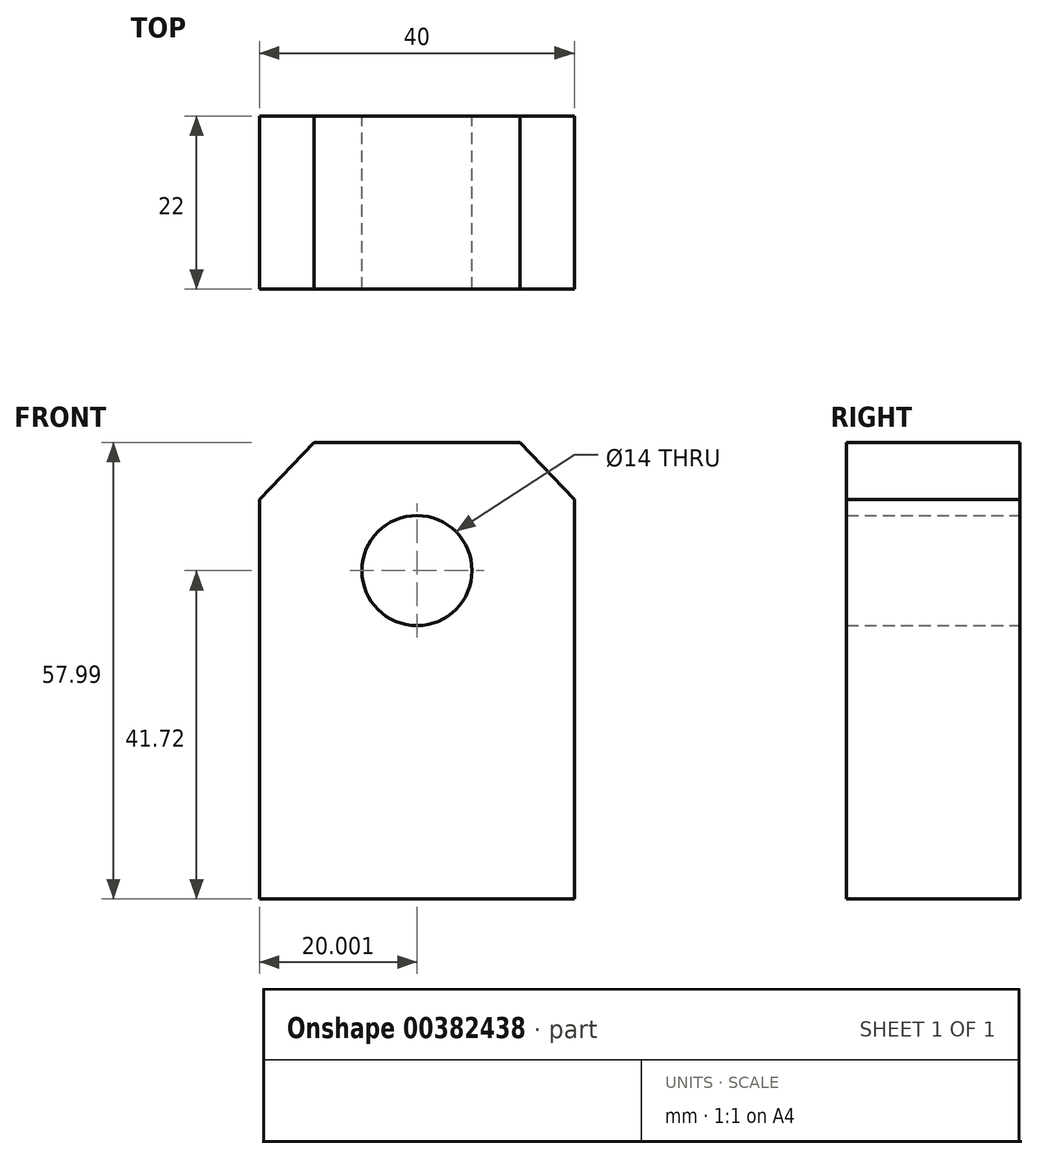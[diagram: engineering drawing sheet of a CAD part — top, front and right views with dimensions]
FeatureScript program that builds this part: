
annotation { "Feature Type Name" : "Feature", "Feature Type Description" : "" }
export const myFeature = defineFeature(function(context is Context, id is Id, definition is map)
    precondition{}
    {
        {
            var Q0;
            Q0=qCreatedBy(makeId("Front.planeOp"),FACE);
            var sketch = newSketch(context, id + "F0", { "sketchPlane" : qUnion([Q0])});
            skLineSegment(sketch, "E0", {"start": v(-35.96, -41.72) * mm, "end": v(-35.96, 9.04) * mm});
            skLineSegment(sketch, "E1", {"start": v(4.04, 9.04) * mm, "end": v(4.04, -41.72) * mm});
            skLineSegment(sketch, "E2", {"start": v(4.04, -41.72) * mm, "end": v(-35.96, -41.72) * mm});
            skLineSegment(sketch, "E3", {"start": v(-35.96, 9.04) * mm, "end": v(-29.05, 16.27) * mm});
            skLineSegment(sketch, "E4", {"start": v(-29.05, 16.27) * mm, "end": v(-2.87, 16.27) * mm});
            skLineSegment(sketch, "E5", {"start": v(-2.87, 16.27) * mm, "end": v(4.04, 9.04) * mm});
            skCircle(sketch, "E6", {"center": v(-15.96, 0) * mm, "radius": 7 * mm});
            skPoint(sketch, "E6.centerSnap0", {"position": v(-15.96, 16.27) * mm});
            skSolve(sketch);
        }
        {
            var Q0;
            Q0=makeQuery(id+"F0.imprint","IMPRINT",FACE,{"disambiguationData":[TD([[makeQuery(id+"F0.imprint","IMPRINT",EDGE,{"derivedFrom":sQuery(id+"F0.wireOp",EDGE,"E0")}),-1.0]])]});
            extrude(context, id + "F1", {"entities" : qUnion([Q0]), "depth" : 22 * mm});
        }
    });
